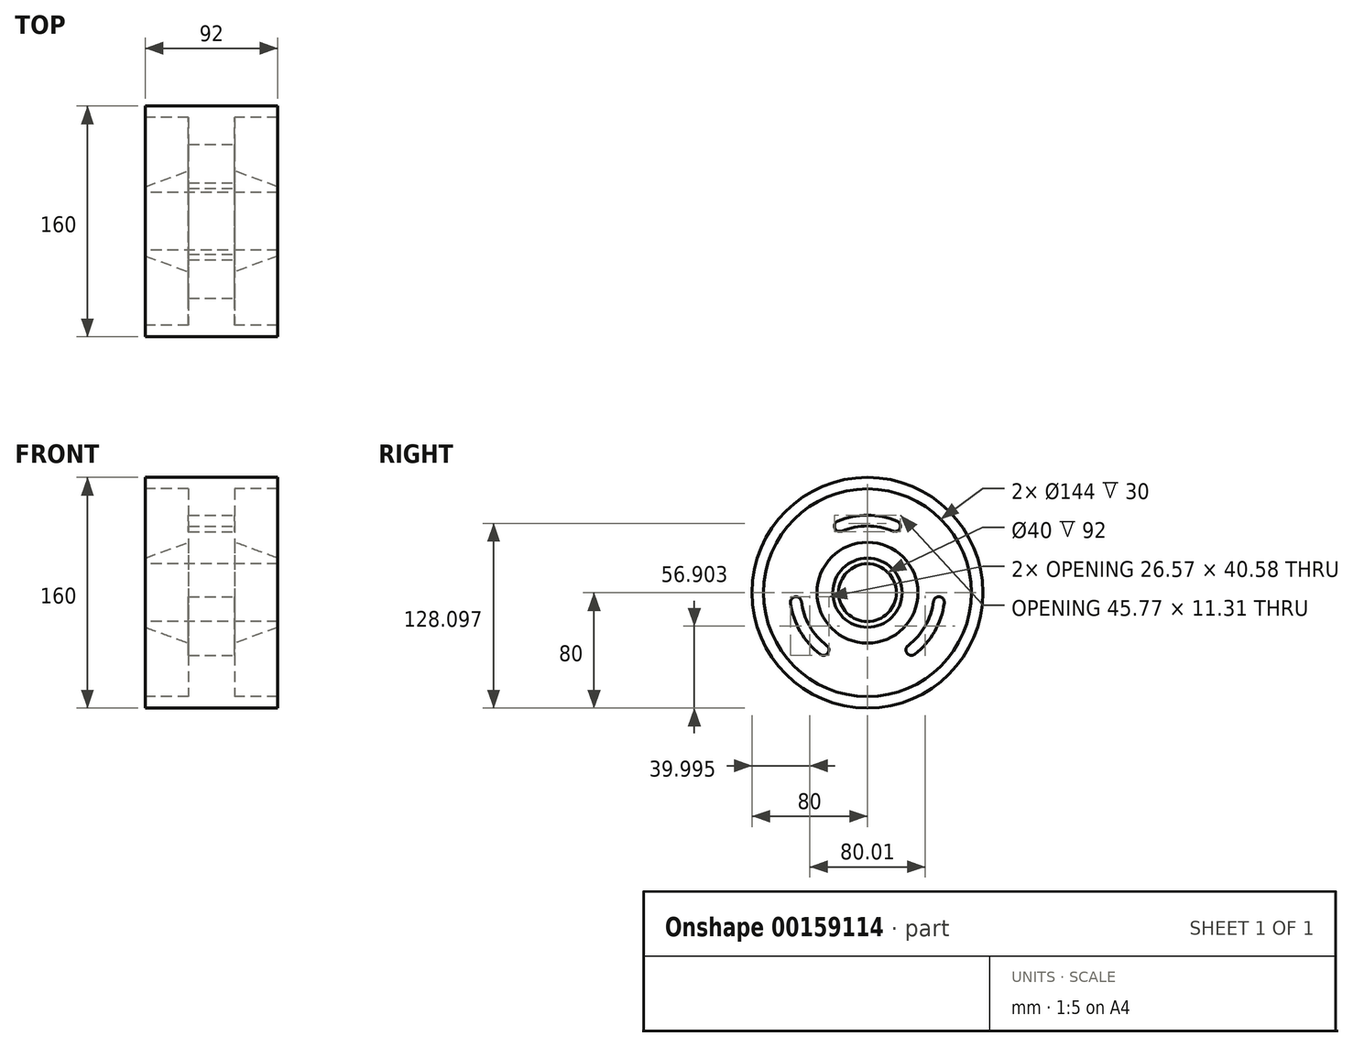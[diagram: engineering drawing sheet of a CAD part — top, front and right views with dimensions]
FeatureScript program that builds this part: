
annotation { "Feature Type Name" : "Feature", "Feature Type Description" : "" }
export const myFeature = defineFeature(function(context is Context, id is Id, definition is map)
    precondition{}
    {
        {
            var Q0;
            Q0=qCreatedBy(makeId("Right.planeOp"),FACE);
            var sketch = newSketch(context, id + "F0", { "sketchPlane" : qUnion([Q0])});
            skCircle(sketch, "E0", {"center": v(0, 0) * mm, "radius": 20 * mm});
            skCircle(sketch, "E1", {"center": v(0, 0) * mm, "radius": 24 * mm});
            skSolve(sketch);
        }
        {
            var Q0;
            Q0 = qSketchRegion(id + "F0", true);
            extrude(context, id + "F1", {"entities" : qUnion([Q0]), "depth" : 92 * mm});
        }
        {
            var Q0;
            Q0=qCreatedBy(makeId("Top.planeOp"),FACE);
            var sketch = newSketch(context, id + "F2", { "sketchPlane" : qUnion([Q0])});
            skLineSegment(sketch, "E2", {"start": v(0, 0) * mm, "end": v(92, 0) * mm, "construction": true});
            skPoint(sketch, "E3", {"position": v(92, 0) * mm});
            skLineSegment(sketch, "E4", {"start": v(0, 20) * mm, "end": v(92, 20) * mm});
            skLineSegment(sketch, "E5", {"start": v(0, 20) * mm, "end": v(0, 24) * mm});
            skLineSegment(sketch, "E6", {"start": v(0, 24) * mm, "end": v(30, 35) * mm});
            skLineSegment(sketch, "E7", {"start": v(92, 20) * mm, "end": v(92, 24) * mm});
            skLineSegment(sketch, "E8", {"start": v(92, 24) * mm, "end": v(62, 35) * mm});
            skLineSegment(sketch, "E9", {"start": v(62, 35) * mm, "end": v(62, 42.35) * mm});
            skLineSegment(sketch, "E10", {"start": v(62, 42.35) * mm, "end": v(30, 42.35) * mm});
            skLineSegment(sketch, "E11", {"start": v(30, 42.35) * mm, "end": v(30, 35) * mm});
            skLineSegment(sketch, "E12", {"start": v(24.75, 50) * mm, "end": v(63.42, 50) * mm, "construction": true});
            skLineSegment(sketch, "E13", {"start": v(30, 56.09) * mm, "end": v(62, 56.09) * mm});
            skLineSegment(sketch, "E14", {"start": v(62, 56.09) * mm, "end": v(62, 72) * mm});
            skLineSegment(sketch, "E15", {"start": v(62, 72) * mm, "end": v(92, 72) * mm});
            skLineSegment(sketch, "E16", {"start": v(92, 72) * mm, "end": v(92, 80) * mm});
            skLineSegment(sketch, "E17", {"start": v(92, 80) * mm, "end": v(0, 80) * mm});
            skLineSegment(sketch, "E18", {"start": v(0, 80) * mm, "end": v(0, 72) * mm});
            skLineSegment(sketch, "E19", {"start": v(0, 72) * mm, "end": v(30, 72) * mm});
            skLineSegment(sketch, "E20", {"start": v(30, 72) * mm, "end": v(30, 56.09) * mm});
            skLineSegment(sketch, "E21", {"start": v(0, 24) * mm, "end": v(92, 24) * mm});
            skPoint(sketch, "E22", {"position": v(46, 20) * mm});
            skLineSegment(sketch, "E23", {"start": v(46, 0) * mm, "end": v(46, 80) * mm, "construction": true});
            skPoint(sketch, "E24", {"position": v(46, 56.09) * mm});
            skPoint(sketch, "E25", {"position": v(46, 42.35) * mm});
            skSolve(sketch);
        }
        {
            var Q0;
            Q0 = qSketchRegion(id + "F2", true);
            var Q1;
            Q1=sQuery(id+"F2.wireOp",EDGE,"E2");
            revolve(context, id + "F3", {"operationType" : NewBodyOperationType.ADD, "entities" : qUnion([Q0]), "axis" : qUnion([Q1]), "revolveType" : RevolveType.FULL});
        }
        {
            var Q0;
            Q0=makeQuery(id+"F3.opRevolve","SWEPT_FACE",FACE,{"disambiguationData":[OSD([sQuery(id+"F2.wireOp",EDGE,"E14")])]});
            var sketch = newSketch(context, id + "F4", { "sketchPlane" : qUnion([Q0])});
            skArc(sketch, "E26.0", {"start": v(22.54, 44.63) * mm, "mid": v(0, 50) * mm, "end": v(-22.54, 44.63) * mm});
            skPoint(sketch, "E27", {"position": v(-19.13, 46.2) * mm});
            skPoint(sketch, "E28", {"position": v(19.13, 46.2) * mm});
            skLineSegment(sketch, "E29", {"start": v(0, 0) * mm, "end": v(0, 56.09) * mm, "construction": true});
            skLineSegment(sketch, "E30", {"start": v(0, 0) * mm, "end": v(19.13, 46.2) * mm, "construction": true});
            skLineSegment(sketch, "E31", {"start": v(0, 0) * mm, "end": v(-20.57, 49.67) * mm, "construction": true});
            skLineSegment(sketch, "E32", {"start": v(-44.17, 0) * mm, "end": v(52.64, 0) * mm, "construction": true});
            skCircle(sketch, "E33", {"center": v(-19.13, 46.2) * mm, "radius": 3.75 * mm});
            skCircle(sketch, "E34", {"center": v(19.13, 46.2) * mm, "radius": 3.75 * mm});
            skArc(sketch, "E35", {"start": v(17.7, 42.73) * mm, "mid": v(0, 46.25) * mm, "end": v(-17.7, 42.73) * mm});
            skArc(sketch, "E36", {"start": v(0, 53.76) * mm, "mid": v(-10.49, 52.72) * mm, "end": v(-20.57, 49.67) * mm});
            skArc(sketch, "E37", {"start": v(20.57, 49.66) * mm, "mid": v(0, 53.75) * mm, "end": v(-20.57, 49.66) * mm});
            skArc(sketch, "E38.1.0", {"start": v(-53.3, -7.02) * mm, "mid": v(-46.55, -26.88) * mm, "end": v(-32.72, -42.64) * mm});
            skCircle(sketch, "E38.1.1", {"center": v(-30.44, -39.67) * mm, "radius": 3.75 * mm});
            skCircle(sketch, "E38.1.2", {"center": v(-49.57, -6.53) * mm, "radius": 3.75 * mm});
            skArc(sketch, "E38.1.3", {"start": v(-45.85, -6.04) * mm, "mid": v(-40.05, -23.13) * mm, "end": v(-28.16, -36.7) * mm});
            skArc(sketch, "E38.2.0", {"start": v(32.72, -42.64) * mm, "mid": v(46.55, -26.88) * mm, "end": v(53.3, -7.02) * mm});
            skCircle(sketch, "E38.2.1", {"center": v(49.57, -6.53) * mm, "radius": 3.75 * mm});
            skCircle(sketch, "E38.2.2", {"center": v(30.44, -39.67) * mm, "radius": 3.75 * mm});
            skArc(sketch, "E38.2.3", {"start": v(28.16, -36.7) * mm, "mid": v(40.05, -23.12) * mm, "end": v(45.85, -6.04) * mm});
            skCircle(sketch, "E39.0", {"center": v(0, 0) * mm, "radius": 56.09 * mm});
            skSolve(sketch);
        }
        {
            var Q0;
            {var subQ6=sQuery(id+"F4.wireOp",EDGE,"E35");Q0=makeQuery(id+"F4.imprint","IMPRINT",FACE,{"disambiguationData":[TD([[makeQuery(id+"F4.imprint","IMPRINT",EDGE,{"derivedFrom":subQ6}),1.0]])]});}
            var Q1;
            Q1=makeQuery(id+"F3.opRevolve","SWEPT_FACE",FACE,{"disambiguationData":[OSD([sQuery(id+"F2.wireOp",EDGE,"E20")])]});
            extrude(context, id + "F5", {"entities" : qUnion([Q0]), "operationType" : NewBodyOperationType.ADD, "endBound" : BoundingType.UP_TO_SURFACE, "oppositeDirection" : true, "endBoundEntityFace" : qUnion([Q1]), "depth" : 25 * mm});
        }
        {
            var Q0;
            Q0=makeQuery(id+"F5.boolean.opBoolean","MERGE",FACE,{"derivedFrom":[makeQuery(id+"F3.opRevolve","SWEPT_FACE",FACE,{"disambiguationData":[OSD([sQuery(id+"F2.wireOp",EDGE,"E14")])]}),makeQuery(id+"F5.opExtrude","CAP_FACE",FACE,{"disambiguationData":[OSD([sQuery(id+"F4.wireOp",EDGE,"E33"),sQuery(id+"F4.wireOp",EDGE,"E34"),sQuery(id+"F4.wireOp",EDGE,"E35"),sQuery(id+"F4.wireOp",EDGE,"E37"),sQuery(id+"F4.wireOp",EDGE,"E38.1.0"),sQuery(id+"F4.wireOp",EDGE,"E38.1.1"),sQuery(id+"F4.wireOp",EDGE,"E38.1.2"),sQuery(id+"F4.wireOp",EDGE,"E38.1.3"),sQuery(id+"F4.wireOp",EDGE,"E38.2.0"),sQuery(id+"F4.wireOp",EDGE,"E38.2.1"),sQuery(id+"F4.wireOp",EDGE,"E38.2.2"),sQuery(id+"F4.wireOp",EDGE,"E38.2.3"),sQuery(id+"F4.wireOp",EDGE,"E39.0")])],"isStart":true})]});
            extrude(context, id + "F6", {"entities" : qUnion([Q0]), "operationType" : NewBodyOperationType.REMOVE, "endBound" : BoundingType.THROUGH_ALL, "oppositeDirection" : true, "depth" : 25 * mm});
        }
    });
